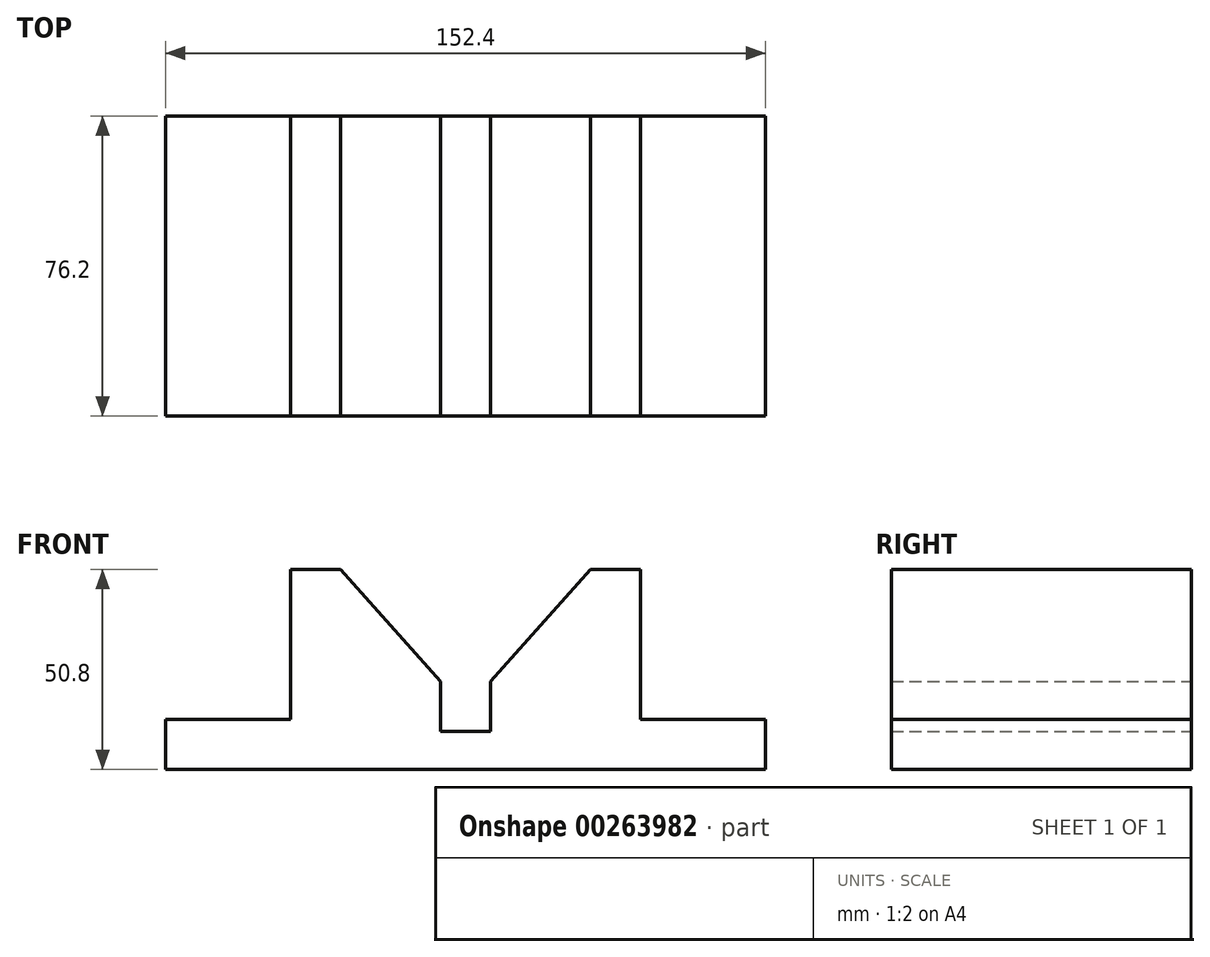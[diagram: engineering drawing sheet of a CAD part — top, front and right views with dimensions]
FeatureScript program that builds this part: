
annotation { "Feature Type Name" : "Feature", "Feature Type Description" : "" }
export const myFeature = defineFeature(function(context is Context, id is Id, definition is map)
    precondition{}
    {
        {
            var Q0;
            Q0=qCreatedBy(makeId("Front.planeOp"),FACE);
            var sketch = newSketch(context, id + "F0", { "sketchPlane" : qUnion([Q0])});
            skLineSegment(sketch, "E0", {"start": v(0, 0) * mm, "end": v(152.4, 0) * mm});
            skLineSegment(sketch, "E1", {"start": v(152.4, 0) * mm, "end": v(152.4, 12.7) * mm});
            skLineSegment(sketch, "E2", {"start": v(152.4, 12.7) * mm, "end": v(120.65, 12.7) * mm});
            skLineSegment(sketch, "E3", {"start": v(120.65, 12.7) * mm, "end": v(120.65, 50.8) * mm});
            skLineSegment(sketch, "E4", {"start": v(120.65, 50.8) * mm, "end": v(107.95, 50.8) * mm});
            skLineSegment(sketch, "E5", {"start": v(107.95, 50.8) * mm, "end": v(82.55, 22.4) * mm});
            skLineSegment(sketch, "E6", {"start": v(82.55, 22.4) * mm, "end": v(82.55, 9.7) * mm});
            skLineSegment(sketch, "E7", {"start": v(82.55, 9.7) * mm, "end": v(69.85, 9.7) * mm});
            skLineSegment(sketch, "E8", {"start": v(69.85, 9.7) * mm, "end": v(69.85, 22.4) * mm});
            skLineSegment(sketch, "E9", {"start": v(69.85, 22.4) * mm, "end": v(44.45, 50.8) * mm});
            skLineSegment(sketch, "E10", {"start": v(44.45, 50.8) * mm, "end": v(31.75, 50.8) * mm});
            skLineSegment(sketch, "E11", {"start": v(31.75, 50.8) * mm, "end": v(31.75, 12.7) * mm});
            skLineSegment(sketch, "E12", {"start": v(31.75, 12.7) * mm, "end": v(0, 12.7) * mm});
            skLineSegment(sketch, "E13", {"start": v(0, 12.7) * mm, "end": v(0, 0) * mm});
            skSolve(sketch);
        }
        {
            var Q0;
            Q0=makeQuery(id+"F0.imprint","IMPRINT",FACE,{"disambiguationData":[TD([[makeQuery(id+"F0.imprint","IMPRINT",EDGE,{"derivedFrom":sQuery(id+"F0.wireOp",EDGE,"E0")}),1.0]])]});
            extrude(context, id + "F1", {"entities" : qUnion([Q0]), "depth" : 76.2 * mm});
        }
    });
